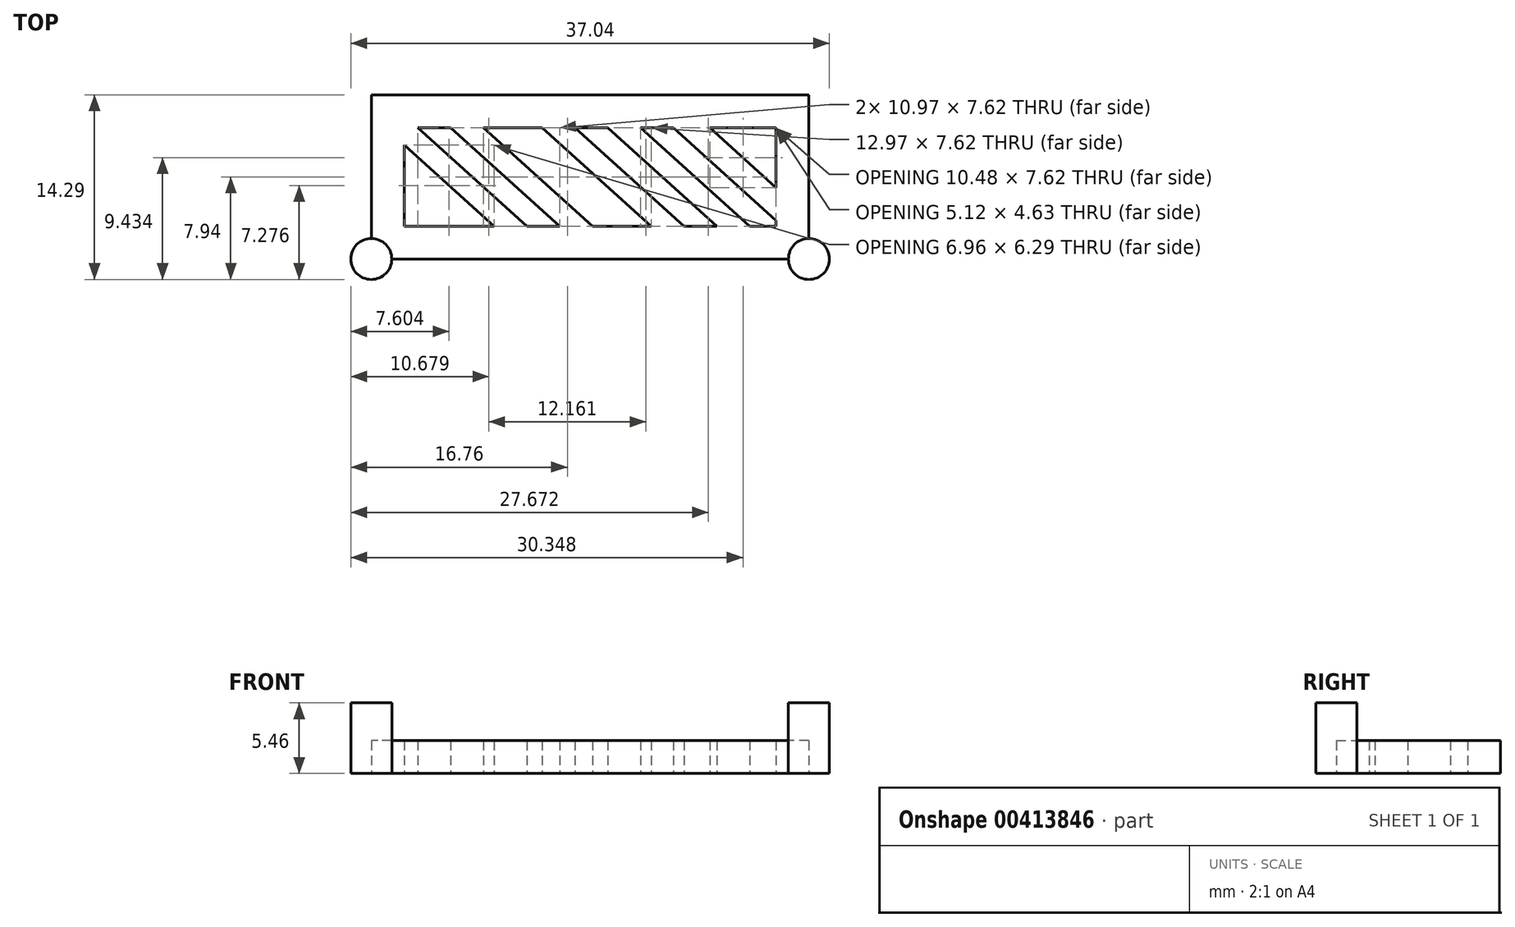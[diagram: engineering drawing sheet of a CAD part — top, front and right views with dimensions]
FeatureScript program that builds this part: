
annotation { "Feature Type Name" : "Feature", "Feature Type Description" : "" }
export const myFeature = defineFeature(function(context is Context, id is Id, definition is map)
    precondition{}
    {
        {
            var Q0;
            Q0=qCreatedBy(makeId("Top.planeOp"),FACE);
            var sketch = newSketch(context, id + "F0", { "sketchPlane" : qUnion([Q0])});
            skLineSegment(sketch, "E0", {"start": v(0, 1.59) * mm, "end": v(0, 12.7) * mm});
            skLineSegment(sketch, "E1", {"start": v(0, 12.7) * mm, "end": v(-33.87, 12.7) * mm});
            skLineSegment(sketch, "E2", {"start": v(-33.87, 12.7) * mm, "end": v(-33.87, 1.59) * mm});
            skLineSegment(sketch, "E3", {"start": v(-32.28, 0) * mm, "end": v(-1.59, 0) * mm});
            skCircle(sketch, "E4", {"center": v(0, 0) * mm, "radius": 1.59 * mm});
            skCircle(sketch, "E5", {"center": v(-33.87, 0) * mm, "radius": 1.59 * mm});
            skLineSegment(sketch, "E6", {"start": v(-33.87, 7.14) * mm, "end": v(-33.87, 9.68) * mm});
            skLineSegment(sketch, "E7", {"start": v(-25.96, 0) * mm, "end": v(-23.42, 0) * mm});
            skLineSegment(sketch, "E8", {"start": v(-27.72, 10.16) * mm, "end": v(-19.28, 2.54) * mm});
            skPoint(sketch, "E8.endSnap0", {"position": v(-16.93, 0) * mm});
            skLineSegment(sketch, "E9", {"start": v(-16.47, 0) * mm, "end": v(-13.93, 0) * mm});
            skLineSegment(sketch, "E10", {"start": v(-16.74, 2.54) * mm, "end": v(-25.18, 10.16) * mm});
            skLineSegment(sketch, "E11.0", {"start": v(-31.33, 10.16) * mm, "end": v(-31.33, 2.54) * mm});
            skLineSegment(sketch, "E11.1", {"start": v(-2.54, 10.16) * mm, "end": v(-31.33, 10.16) * mm});
            skLineSegment(sketch, "E11.2", {"start": v(-2.54, 2.54) * mm, "end": v(-2.54, 10.16) * mm});
            skLineSegment(sketch, "E12.0", {"start": v(-31.33, 2.54) * mm, "end": v(-2.54, 2.54) * mm});
            skLineSegment(sketch, "E13", {"start": v(-25.18, 10.16) * mm, "end": v(-20.64, 10.16) * mm});
            skLineSegment(sketch, "E14", {"start": v(-20.64, 10.16) * mm, "end": v(-12.2, 2.54) * mm});
            skLineSegment(sketch, "E15", {"start": v(-12.2, 2.54) * mm, "end": v(-9.66, 2.54) * mm});
            skLineSegment(sketch, "E16", {"start": v(-9.66, 2.54) * mm, "end": v(-18.1, 10.16) * mm});
            skLineSegment(sketch, "E17", {"start": v(-18.1, 10.16) * mm, "end": v(-15.56, 10.16) * mm});
            skLineSegment(sketch, "E18", {"start": v(-15.56, 10.16) * mm, "end": v(-7.12, 2.54) * mm});
            skLineSegment(sketch, "E19", {"start": v(-7.12, 2.54) * mm, "end": v(-4.58, 2.54) * mm});
            skLineSegment(sketch, "E20", {"start": v(-4.58, 2.54) * mm, "end": v(-13.02, 10.16) * mm});
            skLineSegment(sketch, "E21", {"start": v(-13.02, 10.16) * mm, "end": v(-10.48, 10.16) * mm});
            skLineSegment(sketch, "E22", {"start": v(-10.48, 10.16) * mm, "end": v(-2.54, 2.99) * mm});
            skLineSegment(sketch, "E23", {"start": v(-2.54, 2.99) * mm, "end": v(-2.54, 5.53) * mm});
            skLineSegment(sketch, "E24", {"start": v(-2.54, 5.53) * mm, "end": v(-7.66, 10.16) * mm});
            skLineSegment(sketch, "E25", {"start": v(-27.72, 10.16) * mm, "end": v(-30.26, 10.16) * mm});
            skLineSegment(sketch, "E26", {"start": v(-30.26, 10.16) * mm, "end": v(-21.82, 2.54) * mm});
            skLineSegment(sketch, "E27", {"start": v(-21.82, 2.54) * mm, "end": v(-24.36, 2.54) * mm});
            skLineSegment(sketch, "E28", {"start": v(-24.36, 2.54) * mm, "end": v(-31.33, 8.83) * mm});
            skLineSegment(sketch, "E29", {"start": v(-33.87, 1.59) * mm, "end": v(-33.87, 0) * mm});
            skLineSegment(sketch, "E30", {"start": v(-32.28, 0) * mm, "end": v(-33.87, 0) * mm});
            skLineSegment(sketch, "E31", {"start": v(-1.59, 0) * mm, "end": v(0, 0) * mm});
            skLineSegment(sketch, "E32", {"start": v(0, 0) * mm, "end": v(0, 1.59) * mm});
            skSolve(sketch);
        }
        {
            var Q0;
            {var subQ2=sQuery(id+"F0.wireOp",EDGE,"E31");Q0=makeQuery(id+"F0.imprint","IMPRINT",FACE,{"disambiguationData":[TD([[makeQuery(id+"F0.imprint","IMPRINT",EDGE,{"derivedFrom":subQ2}),1.0]])]});}
            var Q1;
            {var subQ0=sQuery(id+"F0.wireOp",EDGE,"E29");Q1=makeQuery(id+"F0.imprint","IMPRINT",FACE,{"disambiguationData":[TD([[makeQuery(id+"F0.imprint","IMPRINT",EDGE,{"derivedFrom":subQ0}),1.0]])]});}
            var Q2;
            {var subQ32=sQuery(id+"F0.wireOp",EDGE,"E0");Q2=makeQuery(id+"F0.imprint","IMPRINT",FACE,{"disambiguationData":[TD([[makeQuery(id+"F0.imprint","IMPRINT",EDGE,{"derivedFrom":subQ32}),1.0]])]});}
            var Q3;
            {var subQ0=sQuery(id+"F0.wireOp",EDGE,"E8");Q3=makeQuery(id+"F0.imprint","IMPRINT",FACE,{"disambiguationData":[TD([[makeQuery(id+"F0.imprint","IMPRINT",EDGE,{"derivedFrom":subQ0}),1.0]])]});}
            var Q4;
            {var subQ0=sQuery(id+"F0.wireOp",EDGE,"E26");Q4=makeQuery(id+"F0.imprint","IMPRINT",FACE,{"disambiguationData":[TD([[makeQuery(id+"F0.imprint","IMPRINT",EDGE,{"derivedFrom":subQ0}),-1.0]])]});}
            var Q5;
            {var subQ0=sQuery(id+"F0.wireOp",EDGE,"E14");Q5=makeQuery(id+"F0.imprint","IMPRINT",FACE,{"disambiguationData":[TD([[makeQuery(id+"F0.imprint","IMPRINT",EDGE,{"derivedFrom":subQ0}),1.0]])]});}
            var Q6;
            {var subQ0=sQuery(id+"F0.wireOp",EDGE,"E18");Q6=makeQuery(id+"F0.imprint","IMPRINT",FACE,{"disambiguationData":[TD([[makeQuery(id+"F0.imprint","IMPRINT",EDGE,{"derivedFrom":subQ0}),1.0]])]});}
            var Q7;
            {var subQ0=sQuery(id+"F0.wireOp",EDGE,"E22");Q7=makeQuery(id+"F0.imprint","IMPRINT",FACE,{"disambiguationData":[TD([[makeQuery(id+"F0.imprint","IMPRINT",EDGE,{"derivedFrom":subQ0}),1.0]])]});}
            extrude(context, id + "F1", {"entities" : qUnion([Q0, Q1, Q2, Q3, Q4, Q5, Q6, Q7]), "depth" : 2.54 * mm});
        }
        {
            var Q0;
            {var subQ0=sQuery(id+"F0.wireOp",EDGE,"E29");Q0=makeQuery(id+"F0.imprint","IMPRINT",FACE,{"disambiguationData":[TD([[makeQuery(id+"F0.imprint","IMPRINT",EDGE,{"derivedFrom":subQ0}),-1.0]])]});}
            var Q1;
            {var subQ2=sQuery(id+"F0.wireOp",EDGE,"E31");Q1=makeQuery(id+"F0.imprint","IMPRINT",FACE,{"disambiguationData":[TD([[makeQuery(id+"F0.imprint","IMPRINT",EDGE,{"derivedFrom":subQ2}),-1.0]])]});}
            var Q2;
            {var subQ0=sQuery(id+"F0.wireOp",EDGE,"E29");Q2=makeQuery(id+"F0.imprint","IMPRINT",FACE,{"disambiguationData":[TD([[makeQuery(id+"F0.imprint","IMPRINT",EDGE,{"derivedFrom":subQ0}),1.0]])]});}
            var Q3;
            {var subQ2=sQuery(id+"F0.wireOp",EDGE,"E31");Q3=makeQuery(id+"F0.imprint","IMPRINT",FACE,{"disambiguationData":[TD([[makeQuery(id+"F0.imprint","IMPRINT",EDGE,{"derivedFrom":subQ2}),1.0]])]});}
            extrude(context, id + "F2", {"entities" : qUnion([Q0, Q1, Q2, Q3]), "operationType" : NewBodyOperationType.ADD, "depth" : 5.46 * mm});
        }
    });
